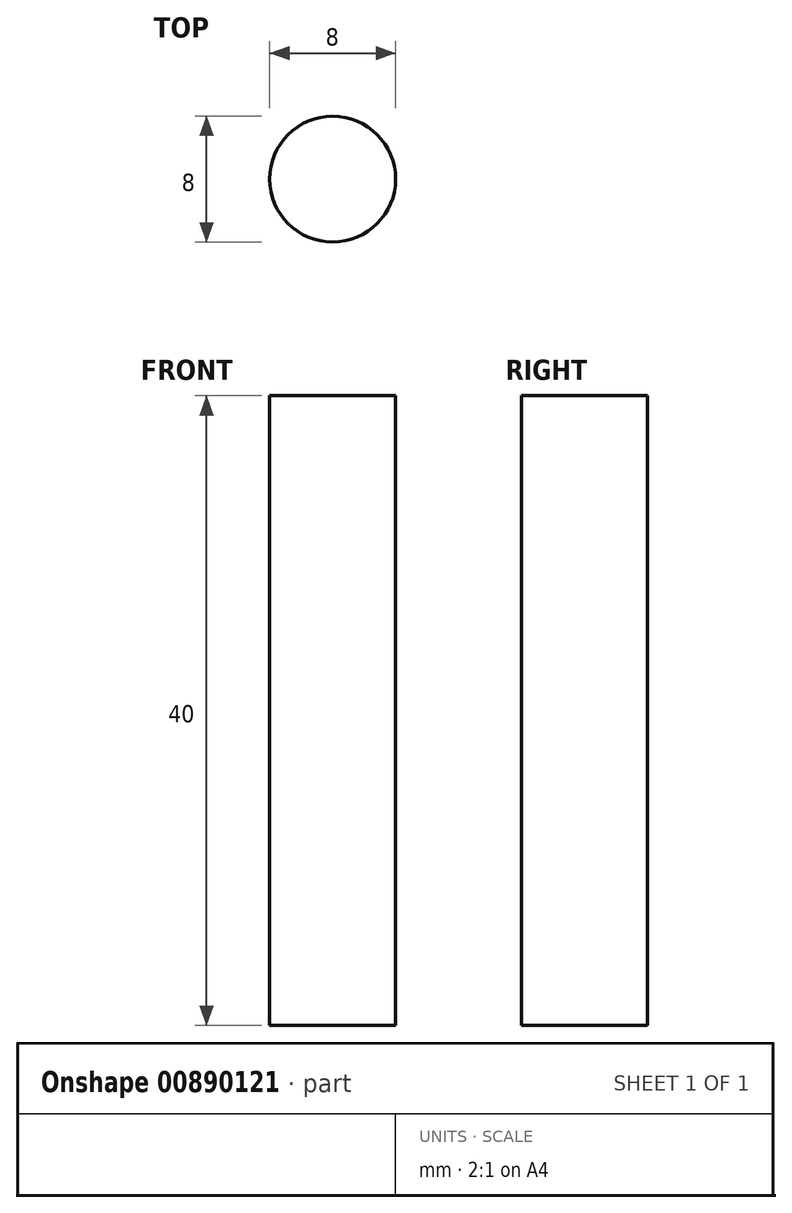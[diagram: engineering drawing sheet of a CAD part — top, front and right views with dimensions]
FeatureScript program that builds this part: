
annotation { "Feature Type Name" : "Feature", "Feature Type Description" : "" }
export const myFeature = defineFeature(function(context is Context, id is Id, definition is map)
    precondition{}
    {
        {
            var Q0;
            Q0=qCreatedBy(makeId("Top.planeOp"),FACE);
            var sketch = newSketch(context, id + "F0", { "sketchPlane" : qUnion([Q0])});
            skCircle(sketch, "E0", {"center": v(0, 0) * mm, "radius": 4 * mm});
            skSolve(sketch);
        }
        {
            var Q0;
            Q0=qSketchRegion(id+"F0",true);
            extrude(context, id + "F1", {"entities" : qUnion([Q0]), "depth" : 40 * mm, "offsetDistance" : 25 * mm});
        }
    });
